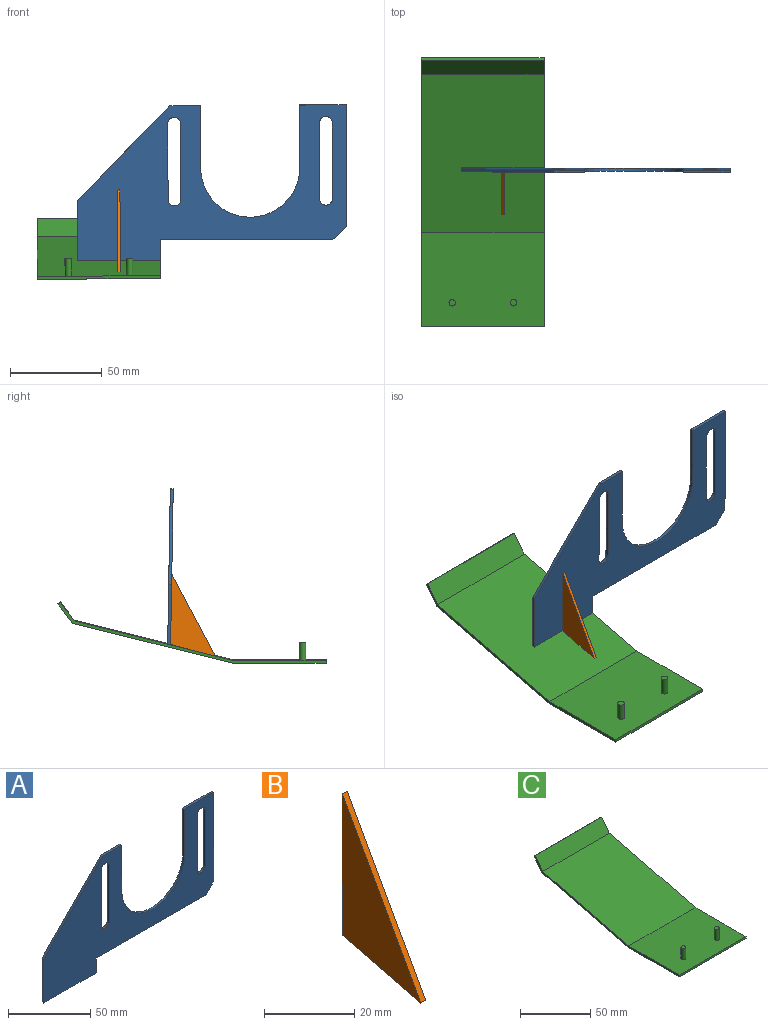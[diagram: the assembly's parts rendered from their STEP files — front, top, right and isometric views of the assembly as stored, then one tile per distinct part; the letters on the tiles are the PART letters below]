
ASSEMBLY  parts=3 mates=2
PART A: 22 faces, bbox 146.6x1.6x84.1 mm
  f0: plane 32.77x1.59mm, normal (-1,0,0), area 51.7mm2, adj f1,f16,f20,f21
  f1: plane 146.56x83.77mm, normal (0,1,0), area 6231.8mm2, adj f0,f2,f3,f4,f5,f6,f7,f8
  f2: cylinder r=3.49mm len=6.99mm, axis (0,1,0), area 17.4mm2, adj f1,f3,f19,f20
  f3: plane 41.28x1.59mm, normal (-1,0,0), area 65.5mm2, adj f1,f2,f4,f20
  f4: cylinder r=3.49mm len=6.99mm, axis (0,1,0), area 17.4mm2, adj f1,f3,f19,f20
  f5: plane 41.28x1.59mm, normal (1,0,0), area 65.5mm2, adj f1,f6,f17,f20
  f6: cylinder r=3.49mm len=6.99mm, axis (0,1,0), area 17.4mm2, adj f1,f5,f7,f20
  f7: plane 41.28x1.59mm, normal (-1,0,0), area 65.5mm2, adj f1,f6,f17,f20
  f8: plane 94.87x1.59mm, normal (0,0,-1), area 150.6mm2, adj f1,f9,f18,f20
  f9: plane 6.74x6.74mm, normal (0.71,0,-0.71), area 15.1mm2, adj f1,f8,f10,f20
  f10: plane 66.29x1.59mm, normal (1,0,0), area 105.2mm2, adj f1,f9,f11,f20
  f11: plane 25.4x1.59mm, normal (0,0,1), area 40.3mm2, adj f1,f10,f12,f20
  f12: plane 34.93x1.59mm, normal (-1,0,0), area 55.4mm2, adj f1,f11,f13,f20
  f13: cylinder r=27.01mm len=53.98mm, axis (0,1,0), area 131.5mm2, adj f1,f12,f14,f20
  f14: plane 34.93x1.59mm, normal (1,0,0), area 55.4mm2, adj f1,f13,f15,f20
  f15: plane 16.51x1.59mm, normal (0,0,1), area 26.2mm2, adj f1,f14,f16,f20
  f16: plane 51.37x50.67mm, normal (-0.71,0,0.7), area 114.6mm2, adj f0,f1,f15,f20
  f17: cylinder r=3.49mm len=6.99mm, axis (0,1,0), area 17.4mm2, adj f1,f5,f7,f20
  f18: plane 11.11x1.59mm, normal (1,0,0), area 17.3mm2, adj f1,f8,f20,f21
  f19: plane 41.28x1.59mm, normal (1,0,0), area 65.5mm2, adj f1,f2,f4,f20
  f20: plane 146.56x84.14mm, normal (0,-1,0), area 6248.3mm2, adj f0,f2,f3,f4,f5,f6,f7,f8
  f21: plane 44.96x1.59mm, normal (0,0.23,-0.97), area 73.3mm2, adj f0,f1,f18,f20
PART B: 5 faces, bbox 1.6x24.6x44.5 mm
  f0: plane 38.35x1.59mm, normal (0,1,0), area 60.9mm2, adj f1,f2,f3,f4
  f1: plane 44.5x24.65mm, normal (0,-0.87,0.48), area 80.8mm2, adj f0,f2,f3,f4
  f2: plane 24.65x6.15mm, normal (0,0.24,-0.97), area 40.3mm2, adj f0,f1,f3,f4
  f3: plane 44.5x24.65mm, normal (-1,0,0), area 472.6mm2, adj f0,f1,f2
  f4: plane 44.5x24.65mm, normal (1,0,0), area 472.6mm2, adj f0,f1,f2
PART C: 14 faces, bbox 66.8x146x33.2 mm
  f0: plane 66.8x10.14mm, normal (0,-0.8,0.6), area 848.4mm2, adj f1,f7,f8,f9
  f1: plane 86.26x66.8mm, normal (0,-0.24,0.97), area 5938.7mm2, adj f0,f2,f8,f9
  f2: plane 66.8x50.8mm, normal (0,0,1), area 3374.2mm2, adj f1,f3,f8,f9,f10,f12
  f3: plane 66.8x1.59mm, normal (0,-1,0), area 106mm2, adj f2,f4,f8,f9
  f4: plane 66.8x51mm, normal (0,0,-1), area 3406.6mm2, adj f3,f5,f8,f9
  f5: plane 86.99x66.8mm, normal (0,0.24,-0.97), area 5989.3mm2, adj f4,f6,f8,f9
  f6: plane 66.8x10.59mm, normal (0,0.8,-0.6), area 885.9mm2, adj f5,f7,f8,f9
  f7: plane 66.8x1.27mm, normal (0,0.6,0.8), area 106mm2, adj f0,f6,f8,f9
  f8: plane 145.97x33.24mm, normal (-1,0,0), area 243.1mm2, adj f0,f1,f2,f3,f4,f5,f6,f7
  f9: plane 145.97x33.24mm, normal (1,0,0), area 243.1mm2, adj f0,f1,f2,f3,f4,f5,f6,f7
  f10: cylinder r=1.75mm len=9.53mm, axis (0,0,-1), area 104.9mm2, adj f2,f11
  f11: plane 3.51x3.51mm, normal (0,0,1), area 9.6mm2, adj f10
  f12: cylinder r=1.75mm len=9.53mm, axis (0,0,-1), area 104.9mm2, adj f2,f13
  f13: plane 3.51x3.51mm, normal (0,0,1), area 9.6mm2, adj f12
PLACE A rot(axis=(0.96,-0.27,0),1deg) t=(67.13,-36.55,1.89)mm
PLACE B rot(axis=(0.96,-0.27,0),1deg) t=(70.52,-36.55,1.9)mm
PLACE C rot(axis=(-0.02,-1,0),0.3deg) t=(67.06,-35.67,1.88)mm fixed
MATE planar A.f21 <-> C.f1  axis (0,0.24,-0.97) through (-15.25,-36.52,-47.54)mm
MATE planar B.f0 <-> A.f20  axis (0,1,0.02) through (-4.38,-37.31,-47.69)mm
